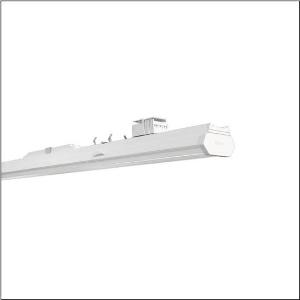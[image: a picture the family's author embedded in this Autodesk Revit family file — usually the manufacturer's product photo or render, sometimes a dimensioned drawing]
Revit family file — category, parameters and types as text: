
# Revit family: licross_r__11_protected_mo_51td11cn49xg_045e
name_source: partatom
category: Lighting Fixtures
units: mm (PartAtom-declared; Revit-internal decimal feet)

## family parameters
Cut with Voids When Loaded = No
Host = Face
Light Source = No
Part Type = Normal
Room Calculation Point = No
Round Connector Dimension = Use Diameter
Shared = No

## types (1)
- --- (1 x LED, 9030 lm, 49.4 W, 4000K)
    Apparent Load = 49 VA
    CIE Flux Codes = 83 94 98 100 100
    Color Rendering = 80
    Color Temperature = 4000K
    Default Elevation = 1800 mm
    Description = Licross® 11 Protected MO, luminaire insert, of sheet steel, galvanised, coil coated, white, length: 1.500mm, width: 90mm, height: 101mm, LED rated luminous flux: 9.030lm, light colour: 840, control gear: ON/OFF Multilumen, CLOi, with plug, 3-pole, with phase selection, mains connection: 220..240V, AC, 50/60Hz, start of lifetime: 49W, end of service life: 55W, halogen-free wiring, primary light control with lens, of plastic, primary optical cover: cover, of PMMA, light emission: direct distribution, primary light characteristic: symmetric, protection rating (complete): IP54, insulation class (complete): insulation class I (protective earthing), certification: CE, ENEC, VDE, UKCA, protection symbol: D if used in an environment with non-conductive dust loads with corresponding accessories, impact resistance: IK06, permissible ambient temperature for indoor applications: -35..+40°C, corresponds to IFS (International Featured Standards) requirements for safety and quality in the food industry, reducing of maximum allowable ambient temperature of 5°C with ceiling mounting, LABS conformity tested according to VDMA 24364:2018-05, packaging unit: 1 piece
    Height = 92 mm
    Lamp = 1 x LED
    Lamp Light Flux = 9030 lm
    Lamp Power = 49.4 W
    Lamp count = 1
    Length = 1500 mm
    Luminous efficacy = 183 lm/W
    Manufacturer = Siteco
    ModVariant = No
    Model = 51TD11CN49XG
    Mounting Place = Ceiling
    Mounting Type = Pendant
    Number of Poles = 1
    OnlyDefault = Yes
    Power Factor = 1
    Product Name = Licross® 11 Protected MO
    Product group = luminaire insert
    ProductGroupID = 901
    Protection Class = Protection class I
    Protection Degree = IP 54
    RLX_Detail_Level = 1
    RLX_Emergency_Light_Flux = 0 lm
    RLX_Emergency_Type = 0
    RLX_Emergency_Type_DB = No
    RlxData = <blob elided: 21873 chars, md5=6465fa9b>
    Socket = socket
    Standby Power = 0 W
    System Light Flux = 9030 lm
    System Power = 49 W
    Type Comments = factory setting: luminous flux: 100 % | (A | C | E) | 113 mA
    Type Image = l_1256145.jpg
    URL = http://relux.com
    VarID = @adj_019279
    Voltage = 0 V
    Weight = 0.00 kg
    Width = 88 mm

## geometry (parser evidence)
native form markers: Blend x4, Sweep x9
no freeform markers — native parametric forms only
